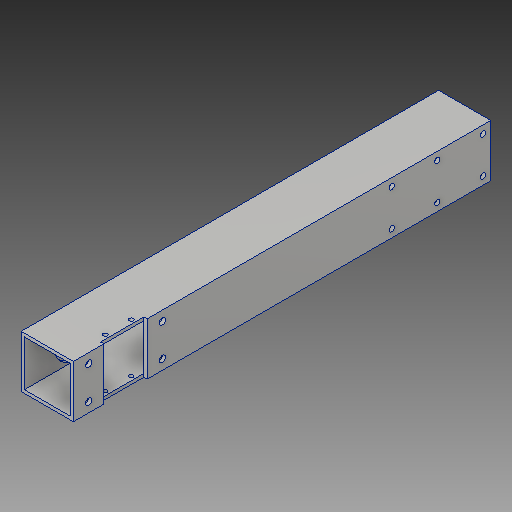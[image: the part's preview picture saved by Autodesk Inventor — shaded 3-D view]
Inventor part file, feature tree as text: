
AUTODESK INVENTOR PART (.ipt)
format: ipt  version: 2019 (Build 230136000, 136)  size: 195,072 bytes
history: native  units: in
note: dims shown in document units (in); Inventor stores cm internally (conversion verified against a paired STEP export)
features: extrude x7, sketch x7, projected_geometry x2
ambient origin geometry x8: Origin, YZ Plane, XZ Plane, XY Plane, X Axis, Y Axis, Z Axis, Center Point
bodies: Solid1 (feature_tree)
feature tree (16):
  extrude  "Extrusion1"  Depth=0.125in
  extrude  "Extrusion2"  Depth=16.0in
  extrude  "Extrusion9"  Depth=3.5in
  extrude  "Extrusion10"  Depth=18.0in TaperAngle=0.0deg
  extrude  "Extrusion11"  Depth=1.654in
  extrude  "Extrusion12"  Depth=0.125in TaperAngle=0.0deg
  extrude  "Extrusion13"  Depth=2.0in
  sketch  "Sketch1"  dims[d0=2.0in d1=0.125in]
  sketch  "Sketch2"  dims[d2=16.0in d3=0.0in d4=0.21in]
  sketch  "Sketch10"  dims[d5=0.3in d6=3.5in]
  projected_geometry  "Projected Loop2"
  sketch  "Sketch11"  dims[d7=0.7in d8=18.0in d9=0.0in]
  sketch  "Sketch12"  dims[d47=2.0in d48=1.654in]
  projected_geometry  "Projected Loop3"
  sketch  "Sketch14"  dims[d49=2.0in d50=0.125in d51=0.0in]
  sketch  "Sketch15"  dims[d52=0.125in d53=0.0in d54=2.0in d55=1.75in d56=0.125in d57=0.0in d67=0.25in d68=1.25in d69=1.0in d70=0.0in d71=1.0in d72=0.0in]
